# Revit family: Morrows DOOR_SINGLE_STANDARD_1428
name_source: partatom
category: Doors
revit_build: Autodesk Revit 2013 (Build: 20121003_2115(x64)
units: mm (PartAtom-declared; Revit-internal decimal feet)

## types (4) — shared parameters
Access Setback Lock Plane = 15 mm  [stored 0.0492126 ft]
Analytic Construction = <None>
Door Frame Material = Metal
Door Handle Material = Door - Handle
Door Leaf Material = Wood - Pine
Door Under Cut = 5 mm  [stored 0.0164042 ft]
Fire Rating = YES
Frame Width = 50 mm  [stored 0.164042 ft]
Function = Interior
Height = 2040 mm
Kick Plate Height = 150 mm
Kick Plate Material = Metal - Stainless Steel
Rebate Depth = 43 mm  [stored 0.141076 ft]
Rebate Width = 15 mm  [stored 0.0492126 ft]
Rough Height = 2100 mm
Thickness = 38 mm  [stored 0.124672 ft]
Wall Closure = By host

## per-type parameters (varying)
| type | Access Setback | Rough Width | Width |
| 850mm Clear - Standard Door | 850 | 1008 mm  [stored 3.30709 ft] | 898 mm  [stored 2.94619 ft] |
| 900mm Clear - Standard Door | 900 | 1058 mm  [stored 3.47113 ft] | 948 mm  [stored 3.11024 ft] |
| 950mm Clear - Standard Door | 950 | 1108 mm  [stored 3.63517 ft] | 998 mm  [stored 3.27428 ft] |
| 1000mm Clear - Standard Door | 1000 | 1158 mm  [stored 3.79921 ft] | 1048 mm  [stored 3.43832 ft] |

note: [stored X ft] marks values corroborated as IEEE doubles in the binary element streams (Revit-internal decimal feet)

## geometry (parser evidence)
native form markers: Blend x6, Sweep x13
no freeform markers — native parametric forms only
